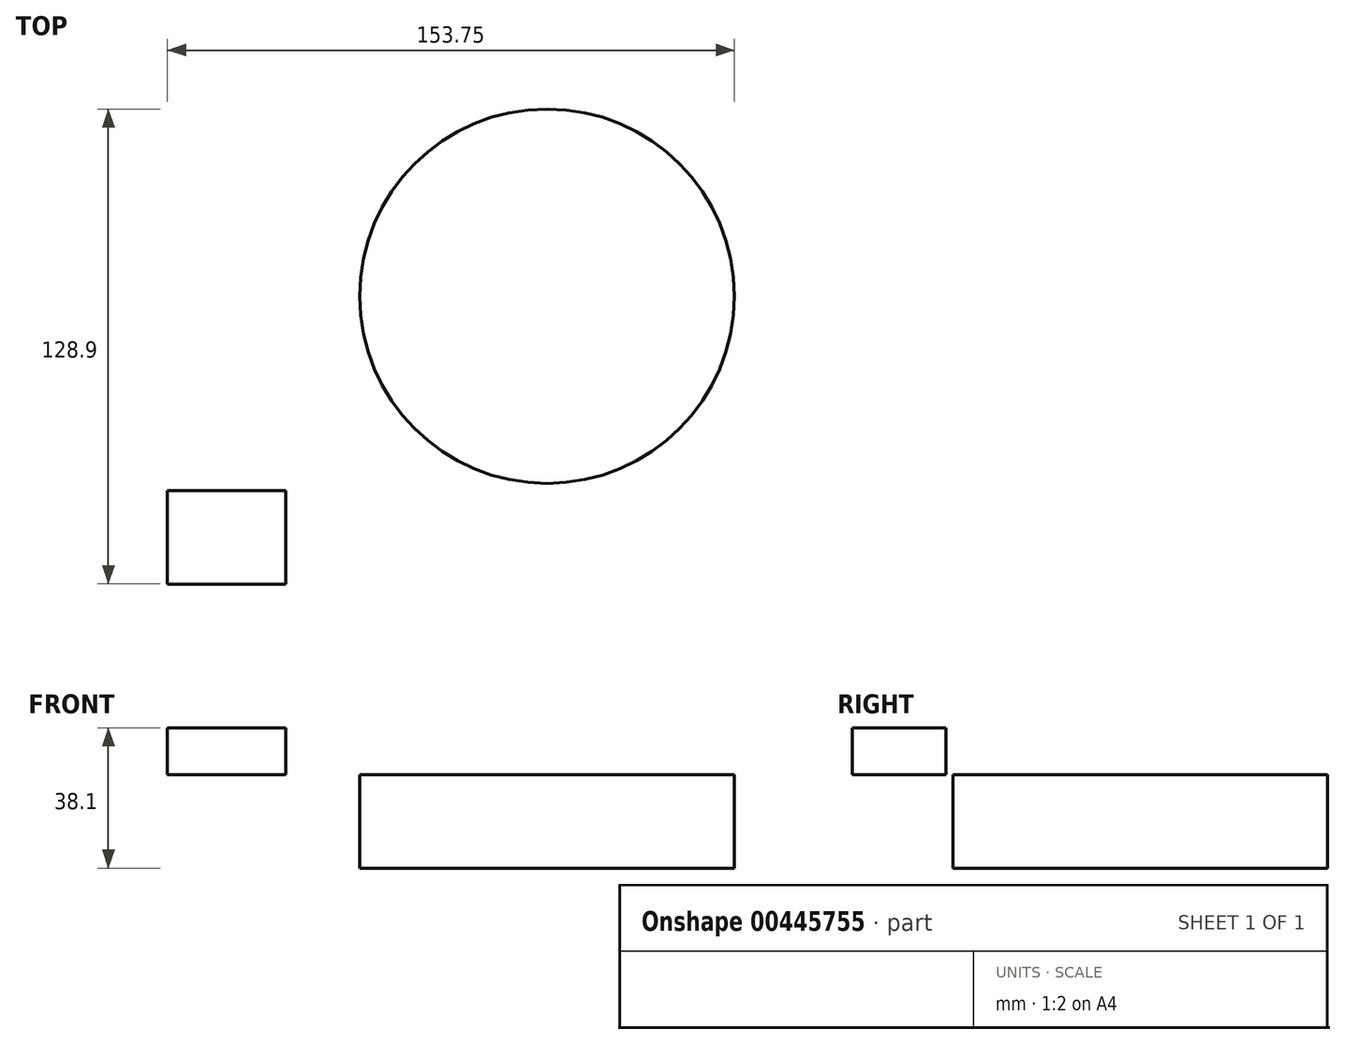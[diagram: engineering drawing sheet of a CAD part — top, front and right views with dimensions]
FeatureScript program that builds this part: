
annotation { "Feature Type Name" : "Feature", "Feature Type Description" : "" }
export const myFeature = defineFeature(function(context is Context, id is Id, definition is map)
    precondition{}
    {
        {
            var Q0;
            Q0=qCreatedBy(makeId("Top.planeOp"),FACE);
            var sketch = newSketch(context, id + "F0", { "sketchPlane" : qUnion([Q0])});
            skCircle(sketch, "E0", {"center": v(-50.8, 0) * mm, "radius": 50.8 * mm});
            skSolve(sketch);
        }
        {
            var Q0;
            Q0 = qSketchRegion(id + "F0", true);
            extrude(context, id + "F1", {"entities" : qUnion([Q0]), "depth" : 25.4 * mm});
        }
        {
            var Q0;
            Q0=makeQuery(id+"F1.opExtrude","CAP_FACE",FACE,{"disambiguationData":[OSD([sQuery(id+"F0.wireOp",EDGE,"E0")])],"isStart":false});
            var sketch = newSketch(context, id + "F2", { "sketchPlane" : qUnion([Q0])});
            skLineSegment(sketch, "E1.bottom", {"start": v(-153.75, -52.76) * mm, "end": v(-121.68, -52.76) * mm});
            skLineSegment(sketch, "E1.top", {"start": v(-153.75, -78.1) * mm, "end": v(-121.68, -78.1) * mm});
            skLineSegment(sketch, "E1.left", {"start": v(-153.75, -52.76) * mm, "end": v(-153.75, -78.1) * mm});
            skLineSegment(sketch, "E1.right", {"start": v(-121.68, -52.76) * mm, "end": v(-121.68, -78.1) * mm});
            skSolve(sketch);
        }
        {
            var Q0;
            Q0 = qSketchRegion(id + "F2", true);
            extrude(context, id + "F3", {"entities" : qUnion([Q0]), "depth" : 12.7 * mm});
        }
    });
